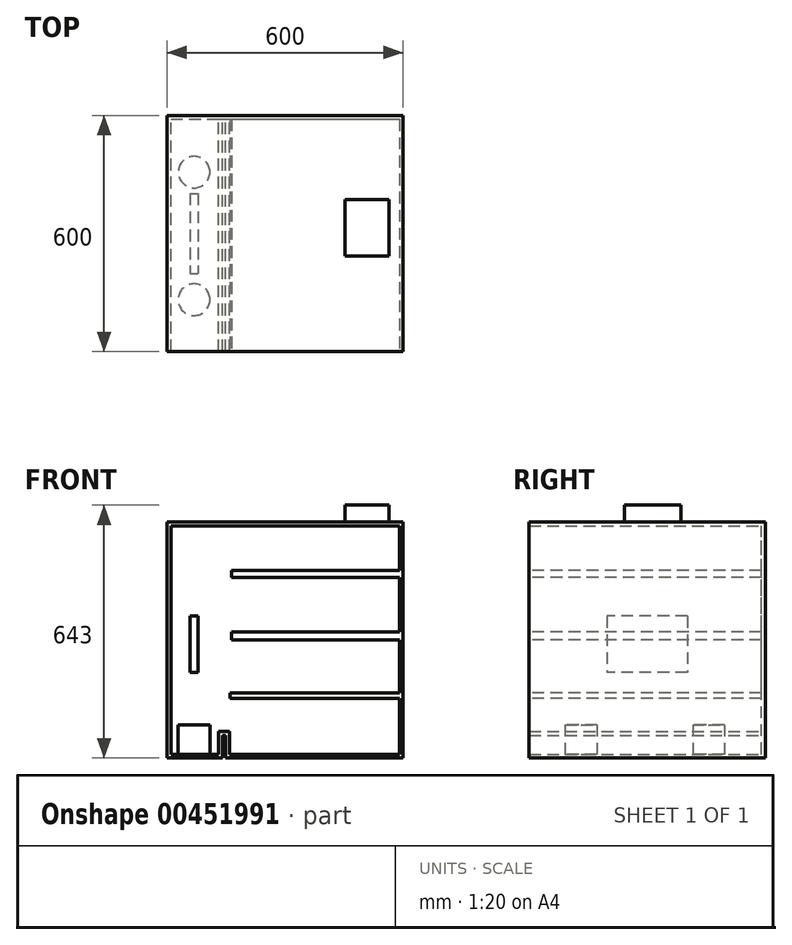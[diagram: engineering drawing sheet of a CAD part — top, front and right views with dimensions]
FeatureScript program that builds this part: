
annotation { "Feature Type Name" : "Feature", "Feature Type Description" : "" }
export const myFeature = defineFeature(function(context is Context, id is Id, definition is map)
    precondition{}
    {
        {
            var Q0;
            Q0=qCreatedBy(makeId("Front.planeOp"),FACE);
            var sketch = newSketch(context, id + "F0", { "sketchPlane" : qUnion([Q0])});
            skLineSegment(sketch, "E0.bottom", {"start": v(0, 0) * mm, "end": v(140.68, 0) * mm});
            skLineSegment(sketch, "E0.top", {"start": v(0, 600) * mm, "end": v(600, 600) * mm});
            skLineSegment(sketch, "E0.left", {"start": v(0, 0) * mm, "end": v(0, 600) * mm});
            skLineSegment(sketch, "E0.right", {"start": v(600, 0) * mm, "end": v(600, 600) * mm});
            skLineSegment(sketch, "E1", {"start": v(140.68, 0) * mm, "end": v(140.68, 58.18) * mm});
            skLineSegment(sketch, "E2", {"start": v(140.68, 58.18) * mm, "end": v(149.04, 58.18) * mm});
            skLineSegment(sketch, "E3", {"start": v(149.04, 58.18) * mm, "end": v(149.04, 0) * mm});
            skLineSegment(sketch, "E4.trimOffspring", {"start": v(149.04, 0) * mm, "end": v(600, 0) * mm});
            skSolve(sketch);
        }
        {
            var Q0;
            Q0 = qSketchRegion(id + "F0", true);
            extrude(context, id + "F1", {"entities" : qUnion([Q0]), "endBound" : BoundingType.SYMMETRIC, "depth" : 600 * mm});
        }
        {
            var Q0;
            Q0=makeQuery(id+"F1.opExtrude","CAP_FACE",FACE,{"disambiguationData":[OSD([sQuery(id+"F0.wireOp",EDGE,"E0.bottom"),sQuery(id+"F0.wireOp",EDGE,"E0.top"),sQuery(id+"F0.wireOp",EDGE,"E0.left"),sQuery(id+"F0.wireOp",EDGE,"E0.right")])],"isStart":false});
            shell(context, id + "F2", {"entities" : qUnion([Q0]), "thickness" : 10 * mm});
        }
        {
            var Q0;
            Q0=makeQuery(id+"F2.opShell","OFFSET_FACE",FACE,{"disambiguationData":[OSD([sQuery(id+"F0.wireOp",EDGE,"E0.bottom")])]});
            var sketch = newSketch(context, id + "F3", { "sketchPlane" : qUnion([Q0])});
            skCircle(sketch, "E5", {"center": v(68.7, -168.24) * mm, "radius": 40.42 * mm});
            skCircle(sketch, "E6", {"center": v(68.68, 155.89) * mm, "radius": 40.23 * mm});
            skSolve(sketch);
        }
        {
            var Q0;
            Q0 = qSketchRegion(id + "F3", true);
            extrude(context, id + "F4", {"entities" : qUnion([Q0]), "operationType" : NewBodyOperationType.ADD, "depth" : 75 * mm});
        }
        {
            var Q0;
            Q0=makeQuery(id+"F1.opExtrude","CAP_FACE",FACE,{"disambiguationData":[OSD([sQuery(id+"F0.wireOp",EDGE,"E0.bottom"),sQuery(id+"F0.wireOp",EDGE,"E0.top"),sQuery(id+"F0.wireOp",EDGE,"E0.left"),sQuery(id+"F0.wireOp",EDGE,"E0.right"),sQuery(id+"F0.wireOp",EDGE,"E1"),sQuery(id+"F0.wireOp",EDGE,"E2"),sQuery(id+"F0.wireOp",EDGE,"E3"),sQuery(id+"F0.wireOp",EDGE,"E4.trimOffspring")])],"isStart":false});
            var sketch = newSketch(context, id + "F5", { "sketchPlane" : qUnion([Q0])});
            skLineSegment(sketch, "E7.bottom", {"start": v(590, 476.53) * mm, "end": v(163.47, 476.53) * mm});
            skLineSegment(sketch, "E7.top", {"start": v(590, 458.6) * mm, "end": v(163.47, 458.6) * mm});
            skLineSegment(sketch, "E7.left", {"start": v(590, 476.53) * mm, "end": v(590, 458.6) * mm});
            skLineSegment(sketch, "E7.right", {"start": v(163.47, 476.53) * mm, "end": v(163.47, 458.6) * mm});
            skPoint(sketch, "E8.oppositeSnap0", {"position": v(590, 300) * mm});
            skLineSegment(sketch, "E8.bottom", {"start": v(590, 320.3) * mm, "end": v(163.47, 320.3) * mm});
            skLineSegment(sketch, "E8.top", {"start": v(590, 300) * mm, "end": v(163.47, 300) * mm});
            skLineSegment(sketch, "E8.left", {"start": v(590, 320.3) * mm, "end": v(590, 300) * mm});
            skLineSegment(sketch, "E8.right", {"start": v(163.47, 320.3) * mm, "end": v(163.47, 300) * mm});
            skLineSegment(sketch, "E9.bottom", {"start": v(590, 165.35) * mm, "end": v(159.62, 165.35) * mm});
            skLineSegment(sketch, "E9.top", {"start": v(590, 151.26) * mm, "end": v(159.62, 151.26) * mm});
            skLineSegment(sketch, "E9.left", {"start": v(590, 165.35) * mm, "end": v(590, 151.26) * mm});
            skLineSegment(sketch, "E9.right", {"start": v(159.62, 165.35) * mm, "end": v(159.62, 151.26) * mm});
            skSolve(sketch);
        }
        {
            var Q0;
            Q0 = qSketchRegion(id + "F5", true);
            var Q1;
            Q1=makeQuery(id+"F2.opShell","OFFSET_FACE",FACE,{"disambiguationData":[OSD([sQuery(id+"F0.wireOp",EDGE,"E0.bottom"),sQuery(id+"F0.wireOp",EDGE,"E0.top"),sQuery(id+"F0.wireOp",EDGE,"E0.left"),sQuery(id+"F0.wireOp",EDGE,"E0.right"),sQuery(id+"F0.wireOp",EDGE,"E1"),sQuery(id+"F0.wireOp",EDGE,"E2"),sQuery(id+"F0.wireOp",EDGE,"E3"),sQuery(id+"F0.wireOp",EDGE,"E4.trimOffspring")])]});
            extrude(context, id + "F6", {"entities" : qUnion([Q0]), "operationType" : NewBodyOperationType.ADD, "endBound" : BoundingType.UP_TO_SURFACE, "oppositeDirection" : true, "endBoundEntityFace" : qUnion([Q1]), "depth" : 25 * mm});
        }
        {
            var Q0;
            Q0=qCreatedBy(makeId("Front.planeOp"),FACE);
            var sketch = newSketch(context, id + "F7", { "sketchPlane" : qUnion([Q0])});
            skLineSegment(sketch, "E10.bottom", {"start": v(58.1, 360.8) * mm, "end": v(78.59, 360.8) * mm});
            skLineSegment(sketch, "E10.top", {"start": v(58.1, 217.37) * mm, "end": v(78.59, 217.37) * mm});
            skLineSegment(sketch, "E10.left", {"start": v(58.1, 360.8) * mm, "end": v(58.1, 217.37) * mm});
            skLineSegment(sketch, "E10.right", {"start": v(78.59, 360.8) * mm, "end": v(78.59, 217.37) * mm});
            skSolve(sketch);
        }
        {
            var Q0;
            Q0 = qSketchRegion(id + "F7", true);
            extrude(context, id + "F8", {"entities" : qUnion([Q0]), "endBound" : BoundingType.SYMMETRIC, "oppositeDirection" : true, "depth" : 204 * mm});
        }
        {
            var Q0;
            Q0=makeQuery(id+"F1.opExtrude","SWEPT_FACE",FACE,{"disambiguationData":[OSD([sQuery(id+"F0.wireOp",EDGE,"E0.top")])]});
            var sketch = newSketch(context, id + "F9", { "sketchPlane" : qUnion([Q0])});
            skLineSegment(sketch, "E11.bottom", {"start": v(563.8, 85.8) * mm, "end": v(452.39, 85.8) * mm});
            skLineSegment(sketch, "E11.top", {"start": v(563.8, -57.63) * mm, "end": v(452.39, -57.63) * mm});
            skLineSegment(sketch, "E11.left", {"start": v(563.8, 85.8) * mm, "end": v(563.8, -57.63) * mm});
            skLineSegment(sketch, "E11.right", {"start": v(452.39, 85.8) * mm, "end": v(452.39, -57.63) * mm});
            skSolve(sketch);
        }
        {
            var Q0;
            Q0 = qSketchRegion(id + "F9", true);
            extrude(context, id + "F10", {"entities" : qUnion([Q0]), "operationType" : NewBodyOperationType.ADD, "depth" : 43 * mm});
        }
    });
